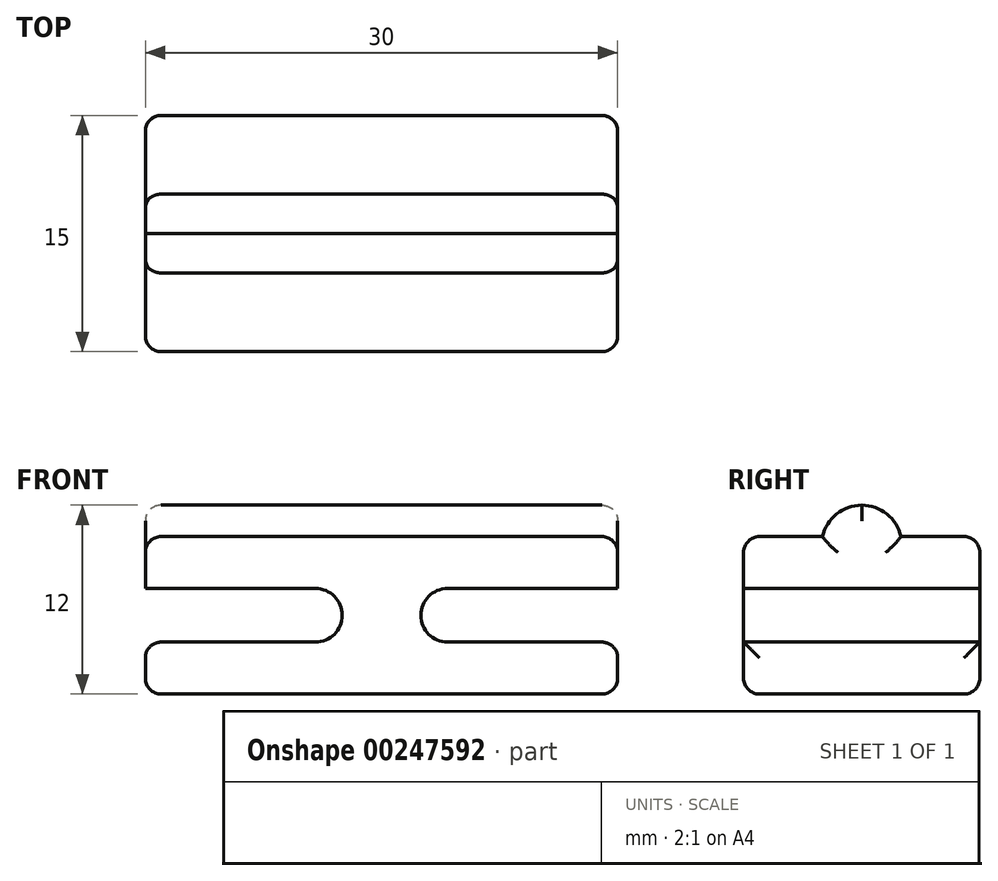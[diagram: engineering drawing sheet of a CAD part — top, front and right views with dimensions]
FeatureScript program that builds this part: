
annotation { "Feature Type Name" : "Feature", "Feature Type Description" : "" }
export const myFeature = defineFeature(function(context is Context, id is Id, definition is map)
    precondition{}
    {
        {
            var Q0;
            Q0=qCreatedBy(makeId("Top.planeOp"),FACE);
            var sketch = newSketch(context, id + "F0", { "sketchPlane" : qUnion([Q0])});
            skLineSegment(sketch, "E0.bottom", {"start": v(0, 0) * mm, "end": v(15, 0) * mm});
            skLineSegment(sketch, "E0.top", {"start": v(0, 15) * mm, "end": v(15, 15) * mm});
            skLineSegment(sketch, "E0.left", {"start": v(0, 0) * mm, "end": v(0, 15) * mm});
            skLineSegment(sketch, "E0.right", {"start": v(15, 0) * mm, "end": v(15, 15) * mm});
            skSolve(sketch);
        }
        {
            var Q0;
            Q0=makeQuery(id+"F0.imprint","IMPRINT",FACE,{"disambiguationData":[TD([[makeQuery(id+"F0.imprint","IMPRINT",EDGE,{"derivedFrom":sQuery(id+"F0.wireOp",EDGE,"E0.bottom")}),1.0]])]});
            extrude(context, id + "F1", {"entities" : qUnion([Q0]), "depth" : 10 * mm});
        }
        {
            var Q0;
            Q0=makeQuery(id+"F1.opExtrude","SWEPT_FACE",FACE,{"disambiguationData":[OSD([sQuery(id+"F0.wireOp",EDGE,"E0.right")])]});
            var sketch = newSketch(context, id + "F2", { "sketchPlane" : qUnion([Q0])});
            skLineSegment(sketch, "E1.bottom", {"start": v(0, 6.7) * mm, "end": v(15, 6.7) * mm});
            skLineSegment(sketch, "E1.top", {"start": v(0, 3.3) * mm, "end": v(15, 3.3) * mm});
            skLineSegment(sketch, "E1.left", {"start": v(0, 6.7) * mm, "end": v(0, 3.3) * mm});
            skLineSegment(sketch, "E1.right", {"start": v(15, 6.7) * mm, "end": v(15, 3.3) * mm});
            skSolve(sketch);
        }
        {
            var Q0;
            Q0 = qSketchRegion(id + "F2", true);
            extrude(context, id + "F3", {"entities" : qUnion([Q0]), "operationType" : NewBodyOperationType.REMOVE, "oppositeDirection" : true, "depth" : 12.5 * mm});
        }
        {
            var Q0;
            Q0=makeQuery(id+"F3.boolean.opBoolean","COPY",EDGE,{"derivedFrom":makeQuery(id+"F3.opExtrude","CAP_EDGE",EDGE,{"disambiguationData":[OSD([sQuery(id+"F2.wireOp",EDGE,"E1.top")])],"isStart":false})});
            var Q1;
            Q1=makeQuery(id+"F3.boolean.opBoolean","COPY",EDGE,{"derivedFrom":makeQuery(id+"F3.opExtrude","CAP_EDGE",EDGE,{"disambiguationData":[OSD([sQuery(id+"F2.wireOp",EDGE,"E1.bottom")])],"isStart":false})});
            fillet(context, id + "F4", {"entities" : qUnion([Q0, Q1]), "radius" : 1.7 * mm, "tangentPropagation" : true, "allowEdgeOverflow" : false});
        }
        {
            var Q0;
            Q0=makeQuery(id+"F1.opExtrude","SWEPT_BODY",BODY,{"disambiguationData":[OSD([sQuery(id+"F0.wireOp",EDGE,"E0.bottom"),sQuery(id+"F0.wireOp",EDGE,"E0.top"),sQuery(id+"F0.wireOp",EDGE,"E0.left"),sQuery(id+"F0.wireOp",EDGE,"E0.right")])]});
            var Q1;
            Q1=makeQuery(id+"F1.opExtrude","SWEPT_FACE",FACE,{"disambiguationData":[OSD([sQuery(id+"F0.wireOp",EDGE,"E0.left")])]});
            mirror(context, id + "F5", {"operationType" : NewBodyOperationType.ADD, "entities" : qUnion([Q0]), "mirrorPlane" : qUnion([Q1])});
        }
        {
            var Q0;
            {var subQ1=sQuery(id+"F0.wireOp",EDGE,"E0.right");Q0=makeQuery(id+"F3.boolean.opBoolean","SPLIT",FACE,{"disambiguationData":[TD([makeQuery(id+"F3.opExtrude","SWEPT_FACE",FACE,{"disambiguationData":[OSD([sQuery(id+"F2.wireOp",EDGE,"E1.bottom")])]})])],"derivedFrom":makeQuery(id+"F1.opExtrude","SWEPT_FACE",FACE,{"disambiguationData":[OSD([subQ1])]})});}
            var sketch = newSketch(context, id + "F6", { "sketchPlane" : qUnion([Q0])});
            skLineSegment(sketch, "E2.bottom", {"start": v(5, 10) * mm, "end": v(10, 10) * mm});
            skLineSegment(sketch, "E2.top", {"start": v(5, 12) * mm, "end": v(10, 12) * mm});
            skLineSegment(sketch, "E2.left", {"start": v(5, 10) * mm, "end": v(5, 12) * mm});
            skLineSegment(sketch, "E2.right", {"start": v(10, 10) * mm, "end": v(10, 12) * mm});
            skSolve(sketch);
        }
        {
            var Q0;
            Q0=makeQuery(id+"F6.imprint","IMPRINT",FACE,{"disambiguationData":[TD([[makeQuery(id+"F6.imprint","IMPRINT",EDGE,{"derivedFrom":sQuery(id+"F6.wireOp",EDGE,"E2.bottom")}),1.0]])]});
            var Q1;
            {var subQ1=sQuery(id+"F0.wireOp",EDGE,"E0.right");Q1=makeQuery(id+"F5.opPattern","COPY",FACE,{"derivedFrom":makeQuery(id+"F3.boolean.opBoolean","SPLIT",FACE,{"disambiguationData":[TD([makeQuery(id+"F3.opExtrude","SWEPT_FACE",FACE,{"disambiguationData":[OSD([sQuery(id+"F2.wireOp",EDGE,"E1.bottom")])]})])],"derivedFrom":makeQuery(id+"F1.opExtrude","SWEPT_FACE",FACE,{"disambiguationData":[OSD([subQ1])]})}),"instanceName":"1"});}
            extrude(context, id + "F7", {"entities" : qUnion([Q0]), "operationType" : NewBodyOperationType.ADD, "endBound" : BoundingType.UP_TO_SURFACE, "oppositeDirection" : true, "endBoundEntityFace" : qUnion([Q1]), "depth" : 25 * mm});
        }
        {
            var Q0;
            Q0=makeQuery(id+"F7.opExtrude","SWEPT_EDGE",EDGE,{"disambiguationData":[OSD([sQuery(id+"F6.wireOp",EDGE,"E2.top"),sQuery(id+"F6.wireOp",EDGE,"E2.left")])]});
            var Q1;
            Q1=makeQuery(id+"F7.opExtrude","SWEPT_EDGE",EDGE,{"disambiguationData":[OSD([sQuery(id+"F6.wireOp",EDGE,"E2.top"),sQuery(id+"F6.wireOp",EDGE,"E2.right")])]});
            fillet(context, id + "F8", {"entities" : qUnion([Q0, Q1]), "radius" : 2.6 * mm, "allowEdgeOverflow" : false});
        }
        {
            var Q0;
            Q0=makeQuery(id+"F5.opPattern","COPY",EDGE,{"derivedFrom":makeQuery(id+"F3.boolean.opBoolean","COPY",EDGE,{"derivedFrom":makeQuery(id+"F3.opExtrude","SWEPT_EDGE",EDGE,{"disambiguationData":[OSD([sQuery(id+"F0.wireOp",EDGE,"E0.bottom"),sQuery(id+"F0.wireOp",EDGE,"E0.right"),sQuery(id+"F2.wireOp",EDGE,"E1.top"),sQuery(id+"F2.wireOp",EDGE,"E1.left")])]})}),"instanceName":"1"});
            var Q1;
            Q1=makeQuery(id+"F3.boolean.opBoolean","COPY",EDGE,{"derivedFrom":makeQuery(id+"F3.opExtrude","SWEPT_EDGE",EDGE,{"disambiguationData":[OSD([sQuery(id+"F0.wireOp",EDGE,"E0.bottom"),sQuery(id+"F0.wireOp",EDGE,"E0.right"),sQuery(id+"F2.wireOp",EDGE,"E1.top"),sQuery(id+"F2.wireOp",EDGE,"E1.left")])]})});
            var Q2;
            Q2=makeQuery(id+"F5.opPattern","COPY",EDGE,{"derivedFrom":makeQuery(id+"F3.boolean.opBoolean","COPY",EDGE,{"derivedFrom":makeQuery(id+"F3.opExtrude","CAP_EDGE",EDGE,{"disambiguationData":[OSD([sQuery(id+"F2.wireOp",EDGE,"E1.top")])],"isStart":true})}),"instanceName":"1"});
            var Q3;
            Q3=makeQuery(id+"F5.opPattern","COPY",EDGE,{"derivedFrom":makeQuery(id+"F1.opExtrude","CAP_EDGE",EDGE,{"disambiguationData":[OSD([sQuery(id+"F0.wireOp",EDGE,"E0.right")])],"isStart":true}),"instanceName":"1"});
            var Q4;
            Q4=makeQuery(id+"F5.opPattern","COPY",EDGE,{"derivedFrom":makeQuery(id+"F3.boolean.opBoolean","COPY",EDGE,{"derivedFrom":makeQuery(id+"F3.opExtrude","CAP_EDGE",EDGE,{"disambiguationData":[OSD([sQuery(id+"F2.wireOp",EDGE,"E1.bottom")])],"isStart":true})}),"instanceName":"1"});
            var Q5;
            {var subQ0=makeQuery(id+"F1.opExtrude","CAP_EDGE",EDGE,{"disambiguationData":[OSD([sQuery(id+"F0.wireOp",EDGE,"E0.top")])],"isStart":true});Q5=makeQuery(id+"F5.boolean.opBoolean","MERGE",EDGE,{"derivedFrom":[subQ0,makeQuery(id+"F5.opPattern","COPY",EDGE,{"derivedFrom":subQ0,"instanceName":"1"})]});}
            var Q6;
            Q6=makeQuery(id+"F5.opPattern","COPY",EDGE,{"derivedFrom":makeQuery(id+"F3.boolean.opBoolean","COPY",EDGE,{"derivedFrom":makeQuery(id+"F3.opExtrude","SWEPT_EDGE",EDGE,{"disambiguationData":[OSD([sQuery(id+"F0.wireOp",EDGE,"E0.top"),sQuery(id+"F0.wireOp",EDGE,"E0.right"),sQuery(id+"F2.wireOp",EDGE,"E1.top"),sQuery(id+"F2.wireOp",EDGE,"E1.right")])]})}),"instanceName":"1"});
            var Q7;
            Q7=makeQuery(id+"F3.boolean.opBoolean","COPY",EDGE,{"derivedFrom":makeQuery(id+"F3.opExtrude","SWEPT_EDGE",EDGE,{"disambiguationData":[OSD([sQuery(id+"F0.wireOp",EDGE,"E0.top"),sQuery(id+"F0.wireOp",EDGE,"E0.right"),sQuery(id+"F2.wireOp",EDGE,"E1.bottom"),sQuery(id+"F2.wireOp",EDGE,"E1.right")])]})});
            var Q8;
            Q8=makeQuery(id+"F1.opExtrude","CAP_EDGE",EDGE,{"disambiguationData":[OSD([sQuery(id+"F0.wireOp",EDGE,"E0.right")])],"isStart":true});
            var Q9;
            Q9=makeQuery(id+"F3.boolean.opBoolean","COPY",EDGE,{"derivedFrom":makeQuery(id+"F3.opExtrude","CAP_EDGE",EDGE,{"disambiguationData":[OSD([sQuery(id+"F2.wireOp",EDGE,"E1.bottom")])],"isStart":true})});
            var Q10;
            Q10=makeQuery(id+"F3.boolean.opBoolean","COPY",EDGE,{"derivedFrom":makeQuery(id+"F3.opExtrude","CAP_EDGE",EDGE,{"disambiguationData":[OSD([sQuery(id+"F2.wireOp",EDGE,"E1.top")])],"isStart":true})});
            var Q11;
            {var subQ0=makeQuery(id+"F1.opExtrude","CAP_EDGE",EDGE,{"disambiguationData":[OSD([sQuery(id+"F0.wireOp",EDGE,"E0.bottom")])],"isStart":true});Q11=makeQuery(id+"F5.boolean.opBoolean","MERGE",EDGE,{"derivedFrom":[subQ0,makeQuery(id+"F5.opPattern","COPY",EDGE,{"derivedFrom":subQ0,"instanceName":"1"})]});}
            var Q12;
            {var subQ0=sQuery(id+"F0.wireOp",EDGE,"E0.right");var subQ1=sQuery(id+"F0.wireOp",EDGE,"E0.top");Q12=makeQuery(id+"F5.opPattern","COPY",EDGE,{"derivedFrom":makeQuery(id+"F3.boolean.opBoolean","SPLIT",EDGE,{"disambiguationData":[TD([makeQuery(id+"F3.opExtrude","SWEPT_FACE",FACE,{"disambiguationData":[OSD([sQuery(id+"F2.wireOp",EDGE,"E1.top")])]})])],"derivedFrom":makeQuery(id+"F1.opExtrude","SWEPT_EDGE",EDGE,{"disambiguationData":[OSD([subQ1,subQ0])]})}),"instanceName":"1"});}
            var Q13;
            {var subQ0=sQuery(id+"F0.wireOp",EDGE,"E0.right");var subQ1=sQuery(id+"F0.wireOp",EDGE,"E0.top");Q13=makeQuery(id+"F3.boolean.opBoolean","SPLIT",EDGE,{"disambiguationData":[TD([makeQuery(id+"F3.opExtrude","SWEPT_FACE",FACE,{"disambiguationData":[OSD([sQuery(id+"F2.wireOp",EDGE,"E1.top")])]})])],"derivedFrom":makeQuery(id+"F1.opExtrude","SWEPT_EDGE",EDGE,{"disambiguationData":[OSD([subQ1,subQ0])]})});}
            var Q14;
            {var subQ0=sQuery(id+"F0.wireOp",EDGE,"E0.bottom");var subQ1=sQuery(id+"F0.wireOp",EDGE,"E0.right");Q14=makeQuery(id+"F3.boolean.opBoolean","SPLIT",EDGE,{"disambiguationData":[TD([makeQuery(id+"F3.opExtrude","SWEPT_FACE",FACE,{"disambiguationData":[OSD([sQuery(id+"F2.wireOp",EDGE,"E1.top")])]})])],"derivedFrom":makeQuery(id+"F1.opExtrude","SWEPT_EDGE",EDGE,{"disambiguationData":[OSD([subQ0,subQ1])]})});}
            var Q15;
            {var subQ0=sQuery(id+"F0.wireOp",EDGE,"E0.bottom");var subQ1=sQuery(id+"F0.wireOp",EDGE,"E0.right");Q15=makeQuery(id+"F5.opPattern","COPY",EDGE,{"derivedFrom":makeQuery(id+"F3.boolean.opBoolean","SPLIT",EDGE,{"disambiguationData":[TD([makeQuery(id+"F3.opExtrude","SWEPT_FACE",FACE,{"disambiguationData":[OSD([sQuery(id+"F2.wireOp",EDGE,"E1.top")])]})])],"derivedFrom":makeQuery(id+"F1.opExtrude","SWEPT_EDGE",EDGE,{"disambiguationData":[OSD([subQ0,subQ1])]})}),"instanceName":"1"});}
            var Q16;
            {var subQ0=sQuery(id+"F6.wireOp",EDGE,"E2.left");var subQ1=sQuery(id+"F6.wireOp",EDGE,"E2.top");var subQ3=sQuery(id+"F0.wireOp",EDGE,"E0.right");Q16=makeQuery(id+"F8.opFillet","BLEND_EDGE",EDGE,{"blendedFrom":[makeQuery(id+"F7.opExtrude","SWEPT_EDGE",EDGE,{"disambiguationData":[OSD([subQ1,subQ0])]}),makeQuery(id+"F7.boolean.opBoolean","MERGE",FACE,{"derivedFrom":[makeQuery(id+"F3.boolean.opBoolean","SPLIT",FACE,{"disambiguationData":[TD([makeQuery(id+"F3.opExtrude","SWEPT_FACE",FACE,{"disambiguationData":[OSD([sQuery(id+"F2.wireOp",EDGE,"E1.bottom")])]})])],"derivedFrom":makeQuery(id+"F1.opExtrude","SWEPT_FACE",FACE,{"disambiguationData":[OSD([subQ3])]})}),makeQuery(id+"F7.opExtrude","CAP_FACE",FACE,{"disambiguationData":[OSD([sQuery(id+"F6.wireOp",EDGE,"E2.bottom"),subQ1,subQ0,sQuery(id+"F6.wireOp",EDGE,"E2.right")])],"isStart":true})]})],"blendedInto":[makeQuery(id+"F7.boolean.opBoolean","MERGE",FACE,{"derivedFrom":[makeQuery(id+"F3.boolean.opBoolean","SPLIT",FACE,{"disambiguationData":[TD([makeQuery(id+"F3.opExtrude","SWEPT_FACE",FACE,{"disambiguationData":[OSD([sQuery(id+"F2.wireOp",EDGE,"E1.bottom")])]})])],"derivedFrom":makeQuery(id+"F1.opExtrude","SWEPT_FACE",FACE,{"disambiguationData":[OSD([subQ3])]})}),makeQuery(id+"F7.opExtrude","CAP_FACE",FACE,{"disambiguationData":[OSD([sQuery(id+"F6.wireOp",EDGE,"E2.bottom"),subQ1,subQ0,sQuery(id+"F6.wireOp",EDGE,"E2.right")])],"isStart":true})]})]});}
            var Q17;
            {var subQ0=sQuery(id+"F0.wireOp",EDGE,"E0.right");var subQ1=sQuery(id+"F0.wireOp",EDGE,"E0.bottom");var subQ3=makeQuery(id+"F1.opExtrude","SWEPT_FACE",FACE,{"disambiguationData":[OSD([subQ1])]});Q17=makeQuery(id+"F7.boolean.opBoolean","SPLIT",EDGE,{"disambiguationData":[TD([subQ3])],"derivedFrom":makeQuery(id+"F1.opExtrude","CAP_EDGE",EDGE,{"disambiguationData":[OSD([subQ0])],"isStart":false})});}
            var Q18;
            {var subQ0=sQuery(id+"F0.wireOp",EDGE,"E0.right");var subQ1=sQuery(id+"F0.wireOp",EDGE,"E0.top");var subQ4=makeQuery(id+"F1.opExtrude","SWEPT_FACE",FACE,{"disambiguationData":[OSD([subQ1])]});Q18=makeQuery(id+"F7.boolean.opBoolean","SPLIT",EDGE,{"disambiguationData":[TD([subQ4])],"derivedFrom":makeQuery(id+"F1.opExtrude","CAP_EDGE",EDGE,{"disambiguationData":[OSD([subQ0])],"isStart":false})});}
            var Q19;
            {var subQ0=sQuery(id+"F0.wireOp",EDGE,"E0.bottom");var subQ1=makeQuery(id+"F1.opExtrude","SWEPT_FACE",FACE,{"disambiguationData":[OSD([subQ0])]});var subQ2=sQuery(id+"F0.wireOp",EDGE,"E0.right");Q19=makeQuery(id+"F7.boolean.opBoolean","SPLIT",EDGE,{"disambiguationData":[TD([subQ1])],"derivedFrom":makeQuery(id+"F5.opPattern","COPY",EDGE,{"derivedFrom":makeQuery(id+"F1.opExtrude","CAP_EDGE",EDGE,{"disambiguationData":[OSD([subQ2])],"isStart":false}),"instanceName":"1"})});}
            var Q20;
            {var subQ1=sQuery(id+"F0.wireOp",EDGE,"E0.right");var subQ2=sQuery(id+"F0.wireOp",EDGE,"E0.top");var subQ4=makeQuery(id+"F1.opExtrude","SWEPT_FACE",FACE,{"disambiguationData":[OSD([subQ2])]});Q20=makeQuery(id+"F7.boolean.opBoolean","SPLIT",EDGE,{"disambiguationData":[TD([subQ4])],"derivedFrom":makeQuery(id+"F5.opPattern","COPY",EDGE,{"derivedFrom":makeQuery(id+"F1.opExtrude","CAP_EDGE",EDGE,{"disambiguationData":[OSD([subQ1])],"isStart":false}),"instanceName":"1"})});}
            var Q21;
            {var subQ0=makeQuery(id+"F1.opExtrude","CAP_EDGE",EDGE,{"disambiguationData":[OSD([sQuery(id+"F0.wireOp",EDGE,"E0.bottom")])],"isStart":false});Q21=makeQuery(id+"F5.boolean.opBoolean","MERGE",EDGE,{"derivedFrom":[subQ0,makeQuery(id+"F5.opPattern","COPY",EDGE,{"derivedFrom":subQ0,"instanceName":"1"})]});}
            var Q22;
            {var subQ0=sQuery(id+"F0.wireOp",EDGE,"E0.bottom");var subQ1=sQuery(id+"F0.wireOp",EDGE,"E0.right");Q22=makeQuery(id+"F5.opPattern","COPY",EDGE,{"derivedFrom":makeQuery(id+"F3.boolean.opBoolean","SPLIT",EDGE,{"disambiguationData":[TD([makeQuery(id+"F3.opExtrude","SWEPT_FACE",FACE,{"disambiguationData":[OSD([sQuery(id+"F2.wireOp",EDGE,"E1.bottom")])]})])],"derivedFrom":makeQuery(id+"F1.opExtrude","SWEPT_EDGE",EDGE,{"disambiguationData":[OSD([subQ0,subQ1])]})}),"instanceName":"1"});}
            var Q23;
            {var subQ0=sQuery(id+"F0.wireOp",EDGE,"E0.bottom");var subQ1=sQuery(id+"F0.wireOp",EDGE,"E0.right");Q23=makeQuery(id+"F3.boolean.opBoolean","SPLIT",EDGE,{"disambiguationData":[TD([makeQuery(id+"F3.opExtrude","SWEPT_FACE",FACE,{"disambiguationData":[OSD([sQuery(id+"F2.wireOp",EDGE,"E1.bottom")])]})])],"derivedFrom":makeQuery(id+"F1.opExtrude","SWEPT_EDGE",EDGE,{"disambiguationData":[OSD([subQ0,subQ1])]})});}
            var Q24;
            {var subQ0=sQuery(id+"F0.wireOp",EDGE,"E0.right");var subQ1=sQuery(id+"F0.wireOp",EDGE,"E0.top");Q24=makeQuery(id+"F5.opPattern","COPY",EDGE,{"derivedFrom":makeQuery(id+"F3.boolean.opBoolean","SPLIT",EDGE,{"disambiguationData":[TD([makeQuery(id+"F3.opExtrude","SWEPT_FACE",FACE,{"disambiguationData":[OSD([sQuery(id+"F2.wireOp",EDGE,"E1.bottom")])]})])],"derivedFrom":makeQuery(id+"F1.opExtrude","SWEPT_EDGE",EDGE,{"disambiguationData":[OSD([subQ1,subQ0])]})}),"instanceName":"1"});}
            var Q25;
            {var subQ0=sQuery(id+"F0.wireOp",EDGE,"E0.right");var subQ1=sQuery(id+"F0.wireOp",EDGE,"E0.top");Q25=makeQuery(id+"F3.boolean.opBoolean","SPLIT",EDGE,{"disambiguationData":[TD([makeQuery(id+"F3.opExtrude","SWEPT_FACE",FACE,{"disambiguationData":[OSD([sQuery(id+"F2.wireOp",EDGE,"E1.bottom")])]})])],"derivedFrom":makeQuery(id+"F1.opExtrude","SWEPT_EDGE",EDGE,{"disambiguationData":[OSD([subQ1,subQ0])]})});}
            var Q26;
            {var subQ0=sQuery(id+"F6.wireOp",EDGE,"E2.right");var subQ1=sQuery(id+"F6.wireOp",EDGE,"E2.top");var subQ3=sQuery(id+"F0.wireOp",EDGE,"E0.right");Q26=makeQuery(id+"F8.opFillet","BLEND_EDGE",EDGE,{"blendedFrom":[makeQuery(id+"F7.opExtrude","SWEPT_EDGE",EDGE,{"disambiguationData":[OSD([subQ1,subQ0])]}),makeQuery(id+"F7.boolean.opBoolean","MERGE",FACE,{"derivedFrom":[makeQuery(id+"F3.boolean.opBoolean","SPLIT",FACE,{"disambiguationData":[TD([makeQuery(id+"F3.opExtrude","SWEPT_FACE",FACE,{"disambiguationData":[OSD([sQuery(id+"F2.wireOp",EDGE,"E1.bottom")])]})])],"derivedFrom":makeQuery(id+"F1.opExtrude","SWEPT_FACE",FACE,{"disambiguationData":[OSD([subQ3])]})}),makeQuery(id+"F7.opExtrude","CAP_FACE",FACE,{"disambiguationData":[OSD([sQuery(id+"F6.wireOp",EDGE,"E2.bottom"),subQ1,sQuery(id+"F6.wireOp",EDGE,"E2.left"),subQ0])],"isStart":true})]})],"blendedInto":[makeQuery(id+"F7.boolean.opBoolean","MERGE",FACE,{"derivedFrom":[makeQuery(id+"F3.boolean.opBoolean","SPLIT",FACE,{"disambiguationData":[TD([makeQuery(id+"F3.opExtrude","SWEPT_FACE",FACE,{"disambiguationData":[OSD([sQuery(id+"F2.wireOp",EDGE,"E1.bottom")])]})])],"derivedFrom":makeQuery(id+"F1.opExtrude","SWEPT_FACE",FACE,{"disambiguationData":[OSD([subQ3])]})}),makeQuery(id+"F7.opExtrude","CAP_FACE",FACE,{"disambiguationData":[OSD([sQuery(id+"F6.wireOp",EDGE,"E2.bottom"),subQ1,sQuery(id+"F6.wireOp",EDGE,"E2.left"),subQ0])],"isStart":true})]})]});}
            var Q27;
            {var subQ0=sQuery(id+"F6.wireOp",EDGE,"E2.right");var subQ1=sQuery(id+"F6.wireOp",EDGE,"E2.top");var subQ3=sQuery(id+"F0.wireOp",EDGE,"E0.right");Q27=makeQuery(id+"F8.opFillet","BLEND_EDGE",EDGE,{"blendedFrom":[makeQuery(id+"F7.opExtrude","SWEPT_EDGE",EDGE,{"disambiguationData":[OSD([subQ1,subQ0])]}),makeQuery(id+"F7.boolean.opBoolean","MERGE",FACE,{"derivedFrom":[makeQuery(id+"F5.opPattern","COPY",FACE,{"derivedFrom":makeQuery(id+"F3.boolean.opBoolean","SPLIT",FACE,{"disambiguationData":[TD([makeQuery(id+"F3.opExtrude","SWEPT_FACE",FACE,{"disambiguationData":[OSD([sQuery(id+"F2.wireOp",EDGE,"E1.bottom")])]})])],"derivedFrom":makeQuery(id+"F1.opExtrude","SWEPT_FACE",FACE,{"disambiguationData":[OSD([subQ3])]})}),"instanceName":"1"}),makeQuery(id+"F7.opExtrude","CAP_FACE",FACE,{"disambiguationData":[OSD([sQuery(id+"F6.wireOp",EDGE,"E2.bottom"),subQ1,sQuery(id+"F6.wireOp",EDGE,"E2.left"),subQ0])],"isStart":false})]})],"blendedInto":[makeQuery(id+"F7.boolean.opBoolean","MERGE",FACE,{"derivedFrom":[makeQuery(id+"F5.opPattern","COPY",FACE,{"derivedFrom":makeQuery(id+"F3.boolean.opBoolean","SPLIT",FACE,{"disambiguationData":[TD([makeQuery(id+"F3.opExtrude","SWEPT_FACE",FACE,{"disambiguationData":[OSD([sQuery(id+"F2.wireOp",EDGE,"E1.bottom")])]})])],"derivedFrom":makeQuery(id+"F1.opExtrude","SWEPT_FACE",FACE,{"disambiguationData":[OSD([subQ3])]})}),"instanceName":"1"}),makeQuery(id+"F7.opExtrude","CAP_FACE",FACE,{"disambiguationData":[OSD([sQuery(id+"F6.wireOp",EDGE,"E2.bottom"),subQ1,sQuery(id+"F6.wireOp",EDGE,"E2.left"),subQ0])],"isStart":false})]})]});}
            var Q28;
            {var subQ0=sQuery(id+"F6.wireOp",EDGE,"E2.left");var subQ1=sQuery(id+"F6.wireOp",EDGE,"E2.top");var subQ3=sQuery(id+"F0.wireOp",EDGE,"E0.right");Q28=makeQuery(id+"F8.opFillet","BLEND_EDGE",EDGE,{"blendedFrom":[makeQuery(id+"F7.opExtrude","SWEPT_EDGE",EDGE,{"disambiguationData":[OSD([subQ1,subQ0])]}),makeQuery(id+"F7.boolean.opBoolean","MERGE",FACE,{"derivedFrom":[makeQuery(id+"F5.opPattern","COPY",FACE,{"derivedFrom":makeQuery(id+"F3.boolean.opBoolean","SPLIT",FACE,{"disambiguationData":[TD([makeQuery(id+"F3.opExtrude","SWEPT_FACE",FACE,{"disambiguationData":[OSD([sQuery(id+"F2.wireOp",EDGE,"E1.bottom")])]})])],"derivedFrom":makeQuery(id+"F1.opExtrude","SWEPT_FACE",FACE,{"disambiguationData":[OSD([subQ3])]})}),"instanceName":"1"}),makeQuery(id+"F7.opExtrude","CAP_FACE",FACE,{"disambiguationData":[OSD([sQuery(id+"F6.wireOp",EDGE,"E2.bottom"),subQ1,subQ0,sQuery(id+"F6.wireOp",EDGE,"E2.right")])],"isStart":false})]})],"blendedInto":[makeQuery(id+"F7.boolean.opBoolean","MERGE",FACE,{"derivedFrom":[makeQuery(id+"F5.opPattern","COPY",FACE,{"derivedFrom":makeQuery(id+"F3.boolean.opBoolean","SPLIT",FACE,{"disambiguationData":[TD([makeQuery(id+"F3.opExtrude","SWEPT_FACE",FACE,{"disambiguationData":[OSD([sQuery(id+"F2.wireOp",EDGE,"E1.bottom")])]})])],"derivedFrom":makeQuery(id+"F1.opExtrude","SWEPT_FACE",FACE,{"disambiguationData":[OSD([subQ3])]})}),"instanceName":"1"}),makeQuery(id+"F7.opExtrude","CAP_FACE",FACE,{"disambiguationData":[OSD([sQuery(id+"F6.wireOp",EDGE,"E2.bottom"),subQ1,subQ0,sQuery(id+"F6.wireOp",EDGE,"E2.right")])],"isStart":false})]})]});}
            var Q29;
            {var subQ0=makeQuery(id+"F1.opExtrude","CAP_EDGE",EDGE,{"disambiguationData":[OSD([sQuery(id+"F0.wireOp",EDGE,"E0.top")])],"isStart":false});Q29=makeQuery(id+"F5.boolean.opBoolean","MERGE",EDGE,{"derivedFrom":[subQ0,makeQuery(id+"F5.opPattern","COPY",EDGE,{"derivedFrom":subQ0,"instanceName":"1"})]});}
            fillet(context, id + "F9", {"entities" : qUnion([Q0, Q1, Q2, Q3, Q4, Q5, Q6, Q7, Q8, Q9, Q10, Q11, Q12, Q13, Q14, Q15, Q16, Q17, Q18, Q19, Q20, Q21, Q22, Q23, Q24, Q25, Q26, Q27, Q28, Q29]), "radius" : 1 * mm, "tangentPropagation" : true, "allowEdgeOverflow" : false});
        }
    });
